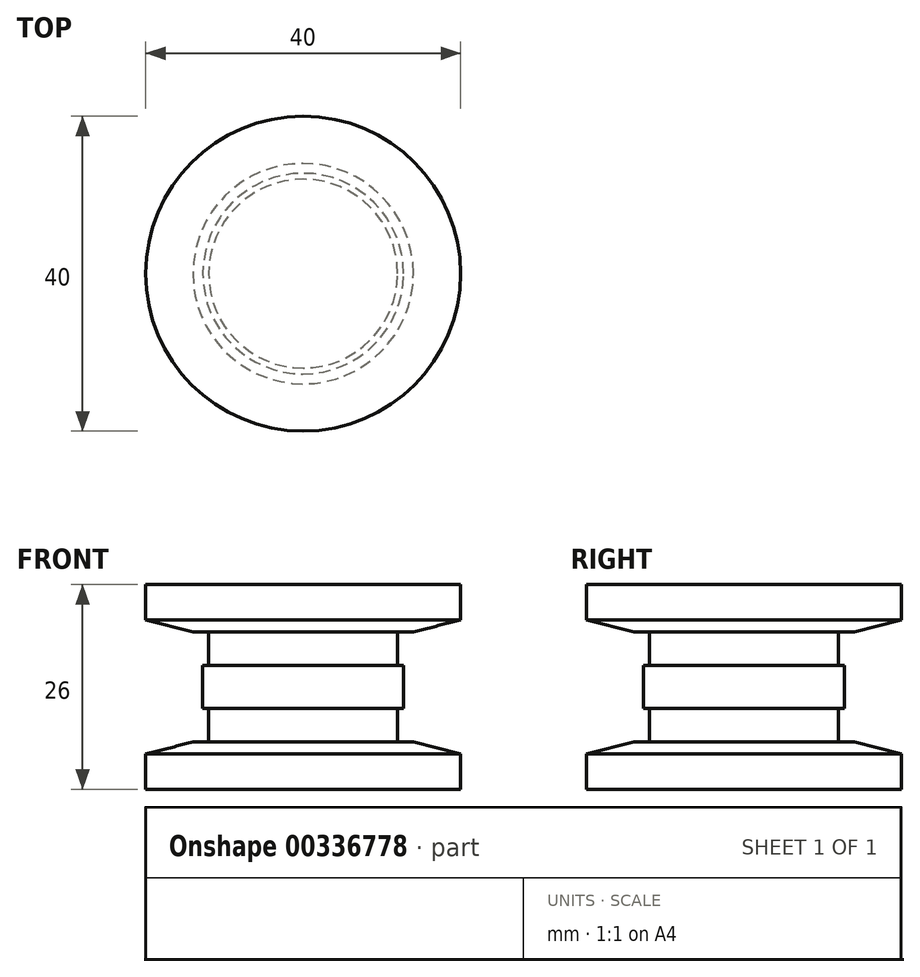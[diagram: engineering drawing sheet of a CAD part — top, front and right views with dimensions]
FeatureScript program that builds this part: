
annotation { "Feature Type Name" : "Feature", "Feature Type Description" : "" }
export const myFeature = defineFeature(function(context is Context, id is Id, definition is map)
    precondition{}
    {
        {
            var Q0;
            Q0=qCreatedBy(makeId("Top.planeOp"),FACE);
            var sketch = newSketch(context, id + "F0", { "sketchPlane" : qUnion([Q0])});
            skCircle(sketch, "E0", {"center": v(0, 0) * mm, "radius": 12.75 * mm});
            skSolve(sketch);
        }
        {
            var Q0;
            Q0 = qSketchRegion(id + "F0", true);
            extrude(context, id + "F1", {"entities" : qUnion([Q0]), "endBound" : BoundingType.SYMMETRIC, "depth" : 5.5 * mm});
        }
        {
            var Q0;
            Q0=makeQuery(id+"F1.opExtrude","CAP_FACE",FACE,{"disambiguationData":[OSD([sQuery(id+"F0.wireOp",EDGE,"E0")])],"isStart":false});
            var sketch = newSketch(context, id + "F2", { "sketchPlane" : qUnion([Q0])});
            skCircle(sketch, "E1", {"center": v(0, 0) * mm, "radius": 12 * mm});
            skSolve(sketch);
        }
        {
            var Q0;
            Q0 = qSketchRegion(id + "F2", true);
            extrude(context, id + "F3", {"entities" : qUnion([Q0]), "operationType" : NewBodyOperationType.ADD, "depth" : 4.25 * mm});
        }
        {
            var Q0;
            Q0=makeQuery(id+"F3.opExtrude","CAP_FACE",FACE,{"disambiguationData":[OSD([sQuery(id+"F2.wireOp",EDGE,"E1")])],"isStart":false});
            var sketch = newSketch(context, id + "F4", { "sketchPlane" : qUnion([Q0])});
            skCircle(sketch, "E2", {"center": v(0, 0) * mm, "radius": 20 * mm});
            skSolve(sketch);
        }
        {
            var Q0;
            Q0 = qSketchRegion(id + "F4", true);
            extrude(context, id + "F5", {"entities" : qUnion([Q0]), "operationType" : NewBodyOperationType.ADD, "depth" : 6 * mm});
        }
        {
            var Q0;
            Q0=makeQuery(id+"F5.opExtrude","CAP_EDGE",EDGE,{"disambiguationData":[OSD([sQuery(id+"F4.wireOp",EDGE,"E2")])],"isStart":true});
            chamfer(context, id + "F6", {"entities" : qUnion([Q0]), "chamferType" : ChamferType.TWO_OFFSETS, "width1" : 1.5 * mm, "oppositeDirection" : false, "width2" : 6 * mm, "tangentPropagation" : true});
        }
        {
            var Q0;
            Q0=makeQuery(id+"F1.opExtrude","CAP_FACE",FACE,{"disambiguationData":[OSD([sQuery(id+"F0.wireOp",EDGE,"E0")])],"isStart":true});
            var sketch = newSketch(context, id + "F7", { "sketchPlane" : qUnion([Q0])});
            skCircle(sketch, "E3", {"center": v(0, 0) * mm, "radius": 12 * mm});
            skSolve(sketch);
        }
        {
            var Q0;
            Q0 = qSketchRegion(id + "F7", true);
            extrude(context, id + "F8", {"entities" : qUnion([Q0]), "operationType" : NewBodyOperationType.ADD, "depth" : 4.25 * mm});
        }
        {
            var Q0;
            Q0=makeQuery(id+"F8.opExtrude","CAP_FACE",FACE,{"disambiguationData":[OSD([sQuery(id+"F7.wireOp",EDGE,"E3")])],"isStart":false});
            var sketch = newSketch(context, id + "F9", { "sketchPlane" : qUnion([Q0])});
            skCircle(sketch, "E4", {"center": v(0, 0) * mm, "radius": 20 * mm});
            skSolve(sketch);
        }
        {
            var Q0;
            Q0 = qSketchRegion(id + "F9", true);
            extrude(context, id + "F10", {"entities" : qUnion([Q0]), "operationType" : NewBodyOperationType.ADD, "depth" : 6 * mm});
        }
        {
            var Q0;
            Q0=makeQuery(id+"F10.opExtrude","CAP_EDGE",EDGE,{"disambiguationData":[OSD([sQuery(id+"F9.wireOp",EDGE,"E4")])],"isStart":true});
            chamfer(context, id + "F11", {"entities" : qUnion([Q0]), "chamferType" : ChamferType.TWO_OFFSETS, "width1" : 1.5 * mm, "oppositeDirection" : false, "width2" : 6 * mm, "tangentPropagation" : true});
        }
    });
